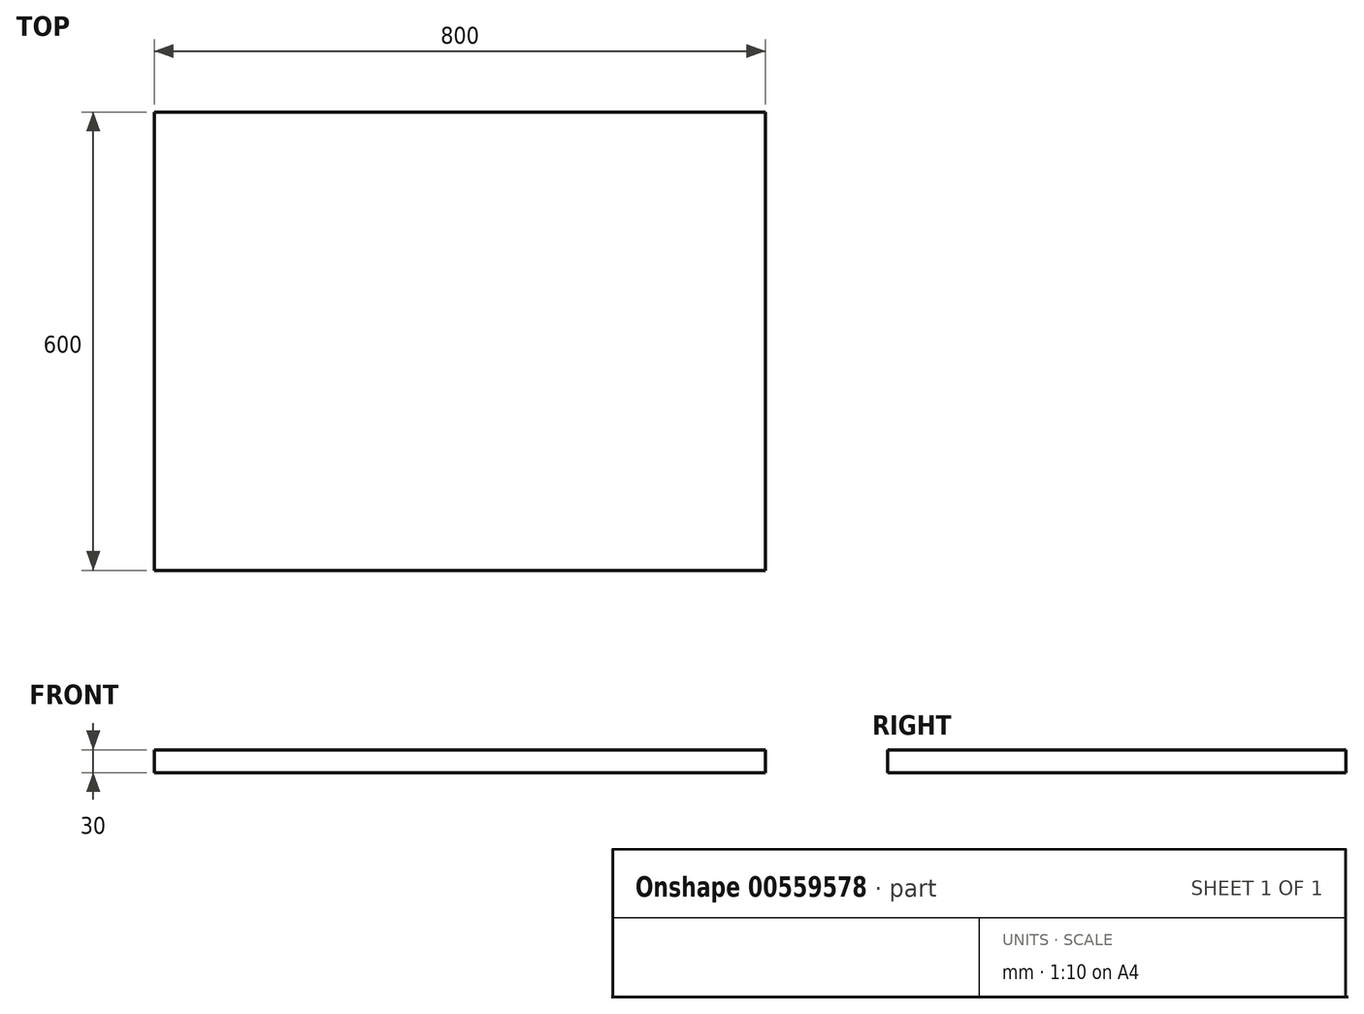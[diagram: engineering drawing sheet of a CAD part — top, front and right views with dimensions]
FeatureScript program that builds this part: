
annotation { "Feature Type Name" : "Feature", "Feature Type Description" : "" }
export const myFeature = defineFeature(function(context is Context, id is Id, definition is map)
    precondition{}
    {
        {
            var Q0;
            Q0=qCreatedBy(makeId("Top.planeOp"),FACE);
            var sketch = newSketch(context, id + "F0", { "sketchPlane" : qUnion([Q0])});
            skLineSegment(sketch, "E0.bottom", {"start": v(-390.64, 419.82) * mm, "end": v(409.36, 419.82) * mm});
            skLineSegment(sketch, "E0.top", {"start": v(-390.64, -180.18) * mm, "end": v(409.36, -180.18) * mm});
            skLineSegment(sketch, "E0.left", {"start": v(-390.64, 419.82) * mm, "end": v(-390.64, -180.18) * mm});
            skLineSegment(sketch, "E0.right", {"start": v(409.36, 419.82) * mm, "end": v(409.36, -180.18) * mm});
            skSolve(sketch);
        }
        {
            var Q0;
            Q0 = qSketchRegion(id + "F0", true);
            extrude(context, id + "F1", {"entities" : qUnion([Q0]), "depth" : 30 * mm, "offsetDistance" : 25 * mm});
        }
    });
